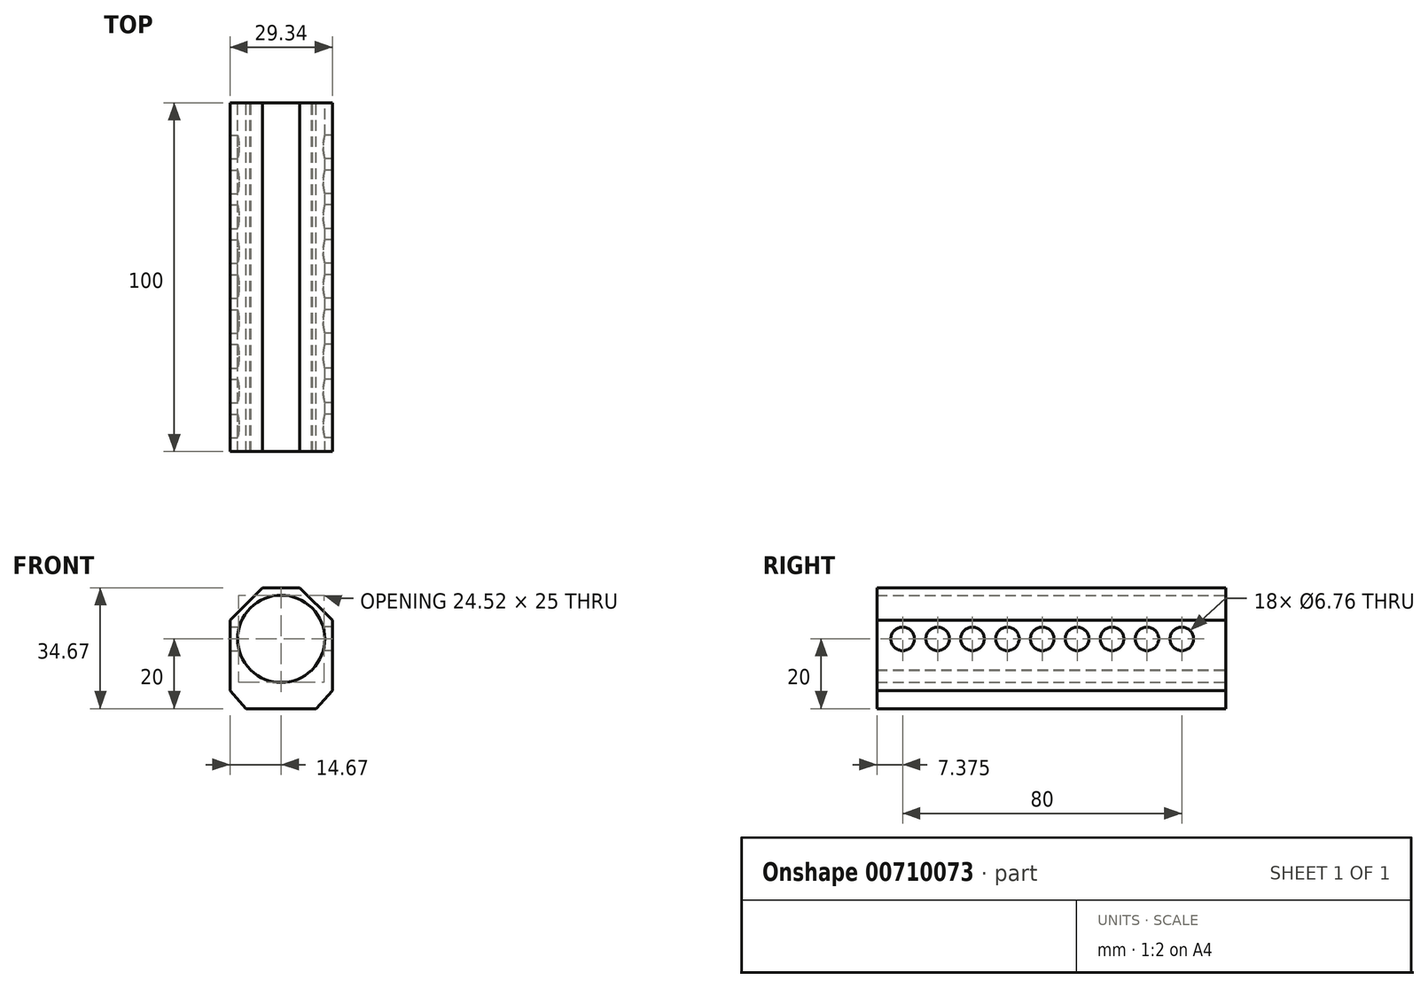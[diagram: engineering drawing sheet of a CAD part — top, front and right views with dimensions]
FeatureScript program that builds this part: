
annotation { "Feature Type Name" : "Feature", "Feature Type Description" : "" }
export const myFeature = defineFeature(function(context is Context, id is Id, definition is map)
    precondition{}
    {
        {
            var Q0;
            Q0=qCreatedBy(makeId("Front.planeOp"),FACE);
            var sketch = newSketch(context, id + "F0", { "sketchPlane" : qUnion([Q0])});
            skCircle(sketch, "E0", {"center": v(0, 0) * mm, "radius": 12.5 * mm});
            skLineSegment(sketch, "E1.bottom", {"start": v(10.02, -20) * mm, "end": v(-10.02, -20) * mm});
            skLineSegment(sketch, "E2", {"start": v(14.67, 5.33) * mm, "end": v(5.33, 14.67) * mm});
            skLineSegment(sketch, "E3", {"start": v(-5.33, 14.67) * mm, "end": v(-14.67, 5.33) * mm});
            skLineSegment(sketch, "E4", {"start": v(-5.33, 14.67) * mm, "end": v(5.33, 14.67) * mm});
            skLineSegment(sketch, "E5", {"start": v(-10.02, -20) * mm, "end": v(-14.67, -14.86) * mm});
            skLineSegment(sketch, "E6", {"start": v(14.67, -14.86) * mm, "end": v(10.02, -20) * mm});
            skLineSegment(sketch, "E7.trimOffspring", {"start": v(-8.84, -8.84) * mm, "end": v(-8.96, -8.96) * mm});
            skLineSegment(sketch, "E8.trimOffspring", {"start": v(8.84, -8.84) * mm, "end": v(8.96, -8.96) * mm});
            skLineSegment(sketch, "E9.trimOffspring", {"start": v(8.71, -8.96) * mm, "end": v(8.96, -8.96) * mm});
            skLineSegment(sketch, "E10.trimOffspring", {"start": v(-8.96, -8.96) * mm, "end": v(-8.71, -8.96) * mm});
            skPoint(sketch, "E11.orphan", {"position": v(0, -20) * mm});
            skPoint(sketch, "E12.orphan", {"position": v(20, -20) * mm});
            skPoint(sketch, "E13.orphan", {"position": v(-20, -20) * mm});
            skPoint(sketch, "E14.orphan", {"position": v(0, -31.08) * mm});
            skPoint(sketch, "E15.orphan", {"position": v(-20, 20) * mm});
            skPoint(sketch, "E16.orphan", {"position": v(20, 20) * mm});
            skPoint(sketch, "E17.orphan", {"position": v(0, 20) * mm});
            skLineSegment(sketch, "E18", {"start": v(-14.67, 5.33) * mm, "end": v(-14.67, -14.86) * mm});
            skLineSegment(sketch, "E19", {"start": v(14.67, -14.86) * mm, "end": v(14.67, 5.33) * mm});
            skPoint(sketch, "E20.orphan", {"position": v(14.67, 14.67) * mm});
            skPoint(sketch, "E21.orphan", {"position": v(20, 0) * mm});
            skPoint(sketch, "E22.end.orphan", {"position": v(14.67, -20.56) * mm});
            skPoint(sketch, "E23.orphan", {"position": v(-20, 0) * mm});
            skSolve(sketch);
        }
        {
            var Q0;
            Q0 = qSketchRegion(id + "F0", true);
            extrude(context, id + "F1", {"entities" : qUnion([Q0]), "depth" : 100 * mm, "offsetDistance" : 25 * mm});
        }
        {
            var Q0;
            Q0=qCreatedBy(makeId("Right.planeOp"),FACE);
            var sketch = newSketch(context, id + "F2", { "sketchPlane" : qUnion([Q0])});
            skCircle(sketch, "E24", {"center": v(-12.63, 0) * mm, "radius": 2.5 * mm});
            skCircle(sketch, "E25", {"center": v(-22.63, 0) * mm, "radius": 2.5 * mm});
            skCircle(sketch, "E26", {"center": v(-32.63, 0) * mm, "radius": 2.5 * mm});
            skCircle(sketch, "E27", {"center": v(-42.63, 0) * mm, "radius": 2.5 * mm});
            skCircle(sketch, "E28", {"center": v(-52.63, 0) * mm, "radius": 2.5 * mm});
            skCircle(sketch, "E29", {"center": v(-62.63, 0) * mm, "radius": 2.5 * mm});
            skCircle(sketch, "E30", {"center": v(-72.63, 0) * mm, "radius": 2.5 * mm});
            skCircle(sketch, "E31", {"center": v(-82.63, 0) * mm, "radius": 2.5 * mm});
            skCircle(sketch, "E32", {"center": v(-92.63, 0) * mm, "radius": 2.5 * mm});
            skPoint(sketch, "E33.orphan", {"position": v(-92.63, 9.97) * mm});
            skPoint(sketch, "E34.start.orphan", {"position": v(-82.63, 9.97) * mm});
            skPoint(sketch, "E35.orphan", {"position": v(-72.63, 9.97) * mm});
            skPoint(sketch, "E36.end.orphan", {"position": v(-72.63, -18.69) * mm});
            skPoint(sketch, "E37.orphan", {"position": v(-62.63, -18.69) * mm});
            skPoint(sketch, "E38.start.orphan", {"position": v(-62.63, 9.68) * mm});
            skPoint(sketch, "E39.start.orphan", {"position": v(-42.63, 9.68) * mm});
            skPoint(sketch, "E40.orphan", {"position": v(-32.63, 9.1) * mm});
            skPoint(sketch, "E41.orphan", {"position": v(-22.63, 9.1) * mm});
            skPoint(sketch, "E42.start.orphan", {"position": v(-12.63, 9.1) * mm});
            skPoint(sketch, "E43.start.orphan", {"position": v(-2.63, 9.1) * mm});
            skSolve(sketch);
        }
        {
            var Q0;
            Q0=sQuery(id+"F2.wireOp",VERTEX,"E32.center");
            var Q1;
            Q1=sQuery(id+"F2.wireOp",VERTEX,"E31.center");
            var Q2;
            Q2=sQuery(id+"F2.wireOp",VERTEX,"E30.center");
            var Q3;
            Q3=sQuery(id+"F2.wireOp",VERTEX,"E29.center");
            var Q4;
            Q4=sQuery(id+"F2.wireOp",VERTEX,"E28.center");
            var Q5;
            Q5=sQuery(id+"F2.wireOp",VERTEX,"E27.center");
            var Q6;
            Q6=sQuery(id+"F2.wireOp",VERTEX,"E26.center");
            var Q7;
            Q7=sQuery(id+"F2.wireOp",VERTEX,"E25.center");
            var Q8;
            Q8=sQuery(id+"F2.wireOp",VERTEX,"E24.center");
            var Q9;
            Q9=makeQuery(id+"F1.opExtrude","SWEPT_BODY",BODY,{"disambiguationData":[OSD([sQuery(id+"F0.wireOp",EDGE,"E0"),sQuery(id+"F0.wireOp",EDGE,"E1.bottom"),sQuery(id+"F0.wireOp",EDGE,"E2"),sQuery(id+"F0.wireOp",EDGE,"E3"),sQuery(id+"F0.wireOp",EDGE,"E4"),sQuery(id+"F0.wireOp",EDGE,"E5"),sQuery(id+"F0.wireOp",EDGE,"E6"),sQuery(id+"F0.wireOp",EDGE,"E7.trimOffspring"),sQuery(id+"F0.wireOp",EDGE,"E8.trimOffspring"),sQuery(id+"F0.wireOp",EDGE,"E9.trimOffspring"),sQuery(id+"F0.wireOp",EDGE,"E10.trimOffspring"),sQuery(id+"F0.wireOp",EDGE,"E18"),sQuery(id+"F0.wireOp",EDGE,"E19")])]});
            hole(context, id + "F3", {"style" : HoleStyle.SIMPLE, "endStyle" : HoleEndStyle.THROUGH, "holeDiameter" : 6.76 * mm, "majorDiameter" : 5 * mm, "isTappedThrough" : true, "tappedDepth" : 12 * mm, "tapClearance" : 3, "startFromSketch" : true, "locations" : qUnion([Q0, Q1, Q2, Q3, Q4, Q5, Q6, Q7, Q8]), "scope" : qUnion([Q9])});
        }
        {
            var Q0;
            Q0=sQuery(id+"F2.wireOp",VERTEX,"E32.center");
            var Q1;
            Q1=sQuery(id+"F2.wireOp",VERTEX,"E31.center");
            var Q2;
            Q2=sQuery(id+"F2.wireOp",VERTEX,"E30.center");
            var Q3;
            Q3=sQuery(id+"F2.wireOp",VERTEX,"E29.center");
            var Q4;
            Q4=sQuery(id+"F2.wireOp",VERTEX,"E28.center");
            var Q5;
            Q5=sQuery(id+"F2.wireOp",VERTEX,"E27.center");
            var Q6;
            Q6=sQuery(id+"F2.wireOp",VERTEX,"E26.center");
            var Q7;
            Q7=sQuery(id+"F2.wireOp",VERTEX,"E25.center");
            var Q8;
            Q8=sQuery(id+"F2.wireOp",VERTEX,"E24.center");
            var Q9;
            Q9=makeQuery(id+"F1.opExtrude","SWEPT_BODY",BODY,{"disambiguationData":[OSD([sQuery(id+"F0.wireOp",EDGE,"E0"),sQuery(id+"F0.wireOp",EDGE,"E1.bottom"),sQuery(id+"F0.wireOp",EDGE,"E2"),sQuery(id+"F0.wireOp",EDGE,"E3"),sQuery(id+"F0.wireOp",EDGE,"E4"),sQuery(id+"F0.wireOp",EDGE,"E5"),sQuery(id+"F0.wireOp",EDGE,"E6"),sQuery(id+"F0.wireOp",EDGE,"E7.trimOffspring"),sQuery(id+"F0.wireOp",EDGE,"E8.trimOffspring"),sQuery(id+"F0.wireOp",EDGE,"E9.trimOffspring"),sQuery(id+"F0.wireOp",EDGE,"E10.trimOffspring"),sQuery(id+"F0.wireOp",EDGE,"E18"),sQuery(id+"F0.wireOp",EDGE,"E19")])]});
            hole(context, id + "F4", {"style" : HoleStyle.SIMPLE, "endStyle" : HoleEndStyle.THROUGH, "oppositeDirection" : true, "holeDiameter" : 6.76 * mm, "majorDiameter" : 5 * mm, "isTappedThrough" : true, "tappedDepth" : 12 * mm, "tapClearance" : 3, "startFromSketch" : true, "locations" : qUnion([Q0, Q1, Q2, Q3, Q4, Q5, Q6, Q7, Q8]), "scope" : qUnion([Q9])});
        }
    });
